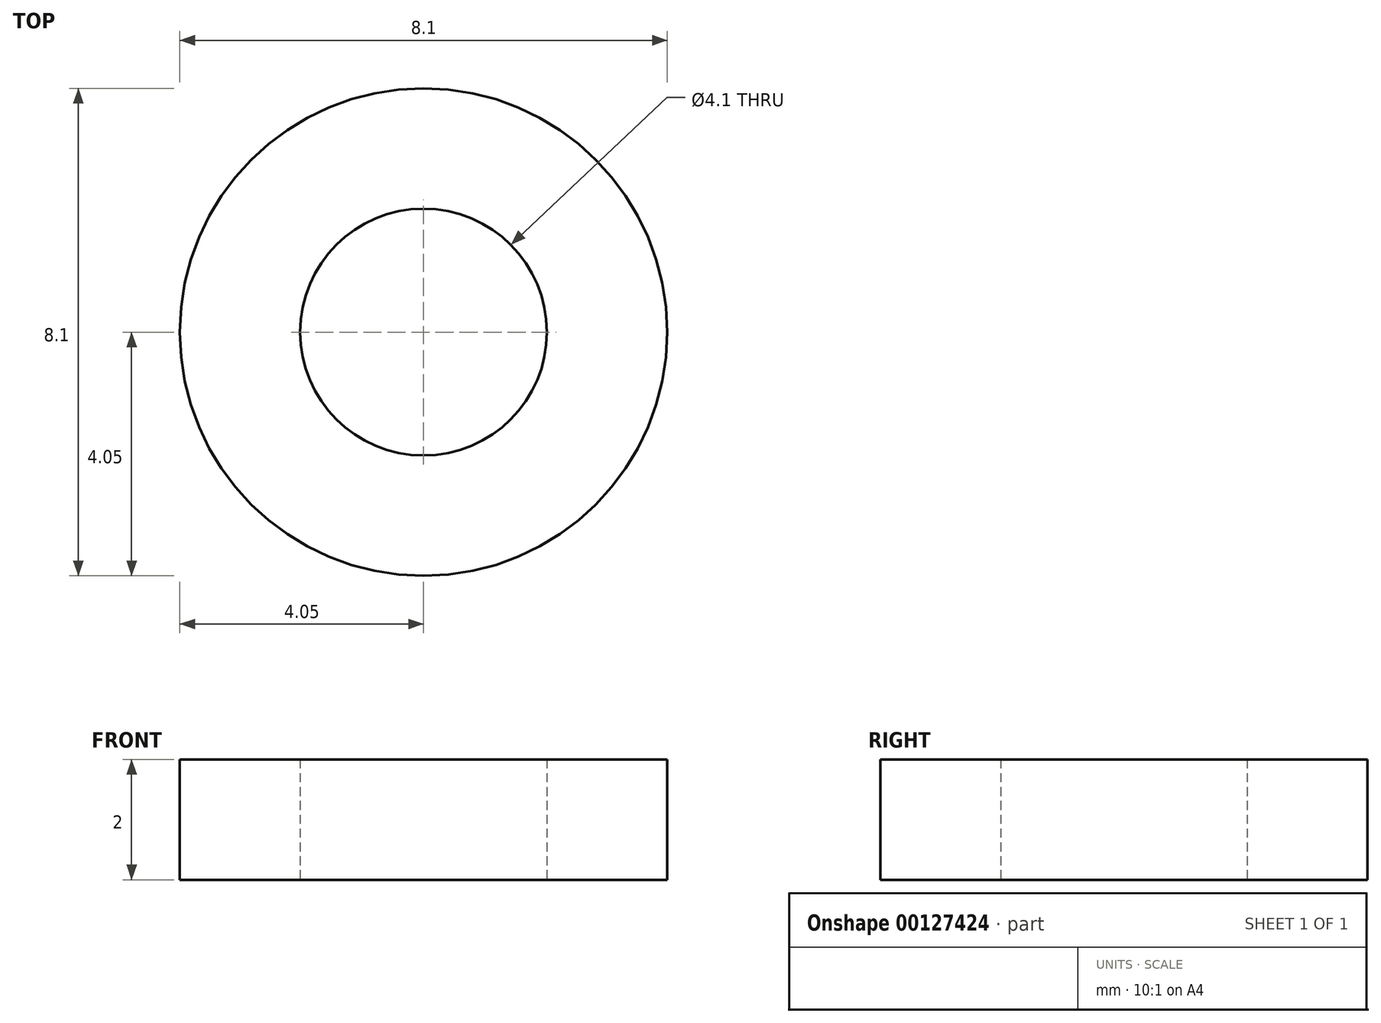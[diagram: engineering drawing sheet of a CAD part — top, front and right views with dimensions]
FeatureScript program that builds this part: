
annotation { "Feature Type Name" : "Feature", "Feature Type Description" : "" }
export const myFeature = defineFeature(function(context is Context, id is Id, definition is map)
    precondition{}
    {
        {
            var Q0;
            Q0=qCreatedBy(makeId("Top.planeOp"),FACE);
            var sketch = newSketch(context, id + "F0", { "sketchPlane" : qUnion([Q0])});
            skCircle(sketch, "E0", {"center": v(0, 0) * mm, "radius": 2.05 * mm});
            skCircle(sketch, "E1", {"center": v(0, 0) * mm, "radius": 4.05 * mm});
            skSolve(sketch);
        }
        {
            var Q0;
            Q0=qSketchRegion(id+"F0",true);
            extrude(context, id + "F1", {"entities" : qUnion([Q0]), "depth" : 2 * mm});
        }
    });
